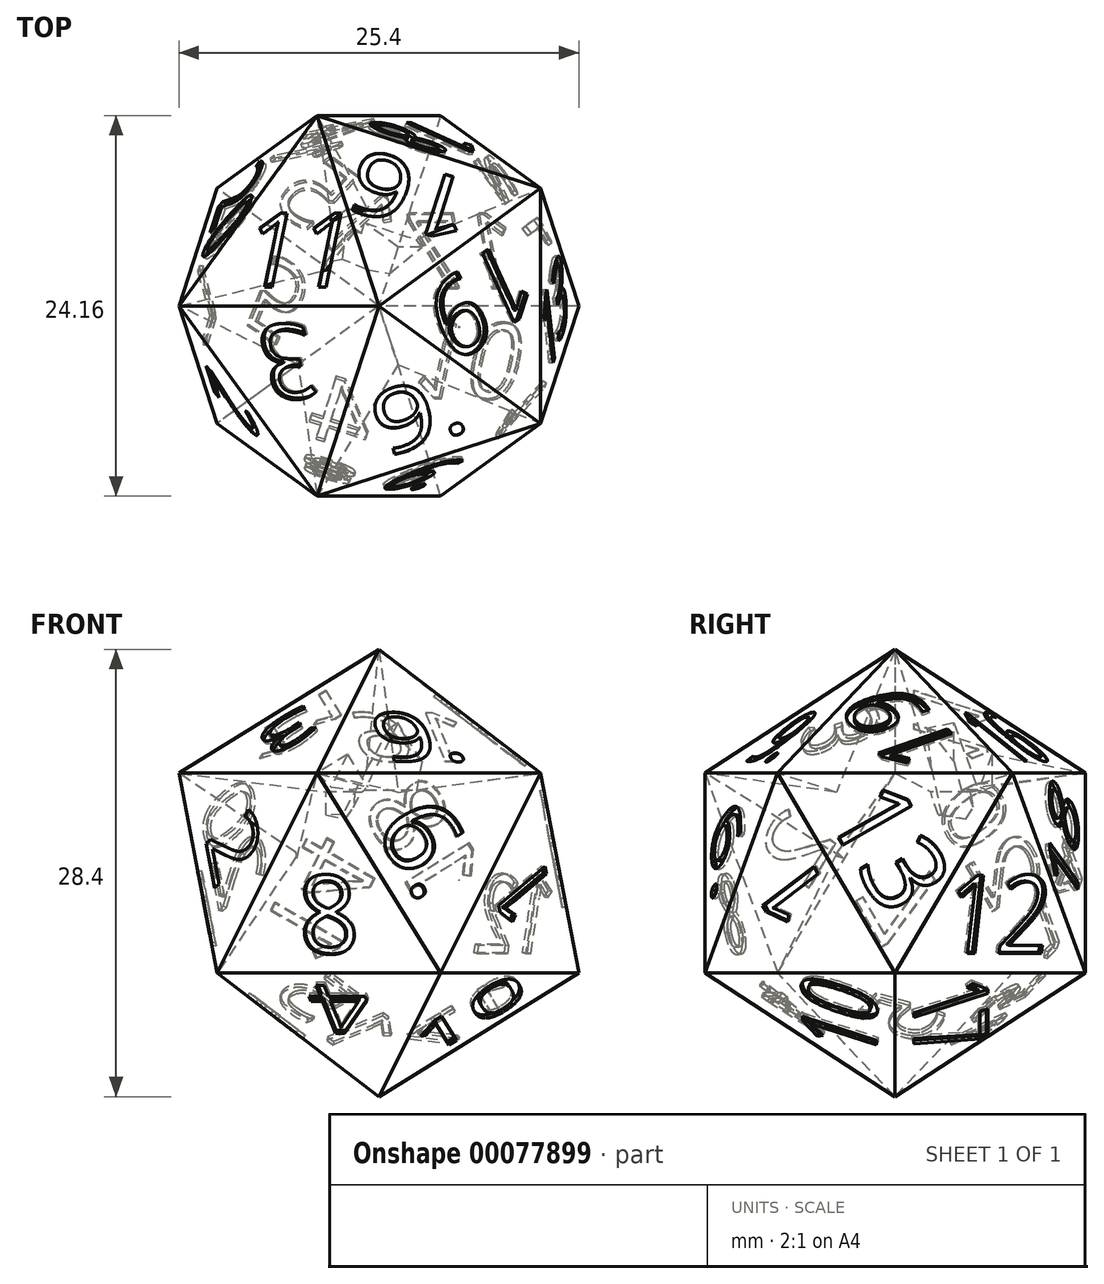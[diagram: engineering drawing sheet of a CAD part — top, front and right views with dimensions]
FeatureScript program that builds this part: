
annotation { "Feature Type Name" : "Feature", "Feature Type Description" : "" }
export const myFeature = defineFeature(function(context is Context, id is Id, definition is map)
    precondition{}
    {
        {
            var Q0;
            Q0=qCreatedBy(makeId("Top.planeOp"),FACE);
            var sketch = newSketch(context, id + "F0", { "sketchPlane" : qUnion([Q0])});
            skCircle(sketch, "E0.cCircle", {"center": v(0, 0) * mm, "radius": 12.7 * mm, "construction": true});
            skLineSegment(sketch, "E0.0", {"start": v(10.27, 7.46) * mm, "end": v(10.27, -7.46) * mm});
            skLineSegment(sketch, "E0.1", {"start": v(10.27, -7.46) * mm, "end": v(-3.92, -12.08) * mm});
            skLineSegment(sketch, "E0.2", {"start": v(-3.92, -12.08) * mm, "end": v(-12.7, 0) * mm});
            skLineSegment(sketch, "E0.3", {"start": v(-12.7, 0) * mm, "end": v(-3.92, 12.08) * mm});
            skLineSegment(sketch, "E0.4", {"start": v(-3.92, 12.08) * mm, "end": v(10.27, 7.46) * mm});
            skLineSegment(sketch, "E1", {"start": v(0, 0) * mm, "end": v(-3.92, -12.08) * mm, "construction": true});
            skSolve(sketch);
        }
        {
            var Q0;
            Q0=qCreatedBy(makeId("Right.planeOp"),FACE);
            var sketch = newSketch(context, id + "F1", { "sketchPlane" : qUnion([Q0])});
            skLineSegment(sketch, "E2", {"start": v(0, 0) * mm, "end": v(0, 7.85) * mm, "construction": true});
            skSolve(sketch);
        }
        {
            var Q0;
            Q0=sQuery(id+"F0.wireOp",VERTEX,"E0.1.start");
            var Q1;
            Q1=sQuery(id+"F0.wireOp",VERTEX,"E0.2.start");
            var Q2;
            Q2=sQuery(id+"F1.wireOp",VERTEX,"E2.end");
            cPlane(context, id + "F2", {"entities" : qUnion([Q0, Q1, Q2]), "cplaneType" : CPlaneType.THREE_POINT, "offset" : 152.4 * mm, "width" : 152.4 * mm, "height" : 152.4 * mm});
        }
        {
            var Q0;
            Q0=qCreatedBy(id+"F2.planeOp",FACE);
            var sketch = newSketch(context, id + "F3", { "sketchPlane" : qUnion([Q0])});
            skPoint(sketch, "E3.0", {"position": v(-5.19, -9.77) * mm});
            skPoint(sketch, "E4.0", {"position": v(9.27, -6.04) * mm});
            skPoint(sketch, "E5.0", {"position": v(-1.2, 4.61) * mm});
            skLineSegment(sketch, "E6", {"start": v(-5.19, -9.77) * mm, "end": v(-1.2, 4.61) * mm});
            skLineSegment(sketch, "E7", {"start": v(9.27, -6.04) * mm, "end": v(-1.2, 4.61) * mm});
            skLineSegment(sketch, "E8", {"start": v(9.27, -6.04) * mm, "end": v(-5.19, -9.77) * mm});
            skLineSegment(sketch, "E9", {"start": v(-3.19, -2.58) * mm, "end": v(9.27, -6.04) * mm, "construction": true});
            skSolve(sketch);
        }
        {
            var Q0;
            Q0=sQuery(id+"F3.wireOp",VERTEX,"E3.0");
            var Q1;
            Q1=sQuery(id+"F0.wireOp",VERTEX,"E0.2.end");
            var Q2;
            Q2=sQuery(id+"F1.wireOp",VERTEX,"E2.end");
            cPlane(context, id + "F4", {"entities" : qUnion([Q0, Q1, Q2]), "cplaneType" : CPlaneType.THREE_POINT, "offset" : 152.4 * mm, "width" : 152.4 * mm, "height" : 152.4 * mm});
        }
        {
            var Q0;
            Q0=qCreatedBy(id+"F4.planeOp",FACE);
            var sketch = newSketch(context, id + "F5", { "sketchPlane" : qUnion([Q0])});
            skPoint(sketch, "E10.0", {"position": v(-11.06, 0) * mm});
            skPoint(sketch, "E11.0", {"position": v(-0.99, -11.02) * mm});
            skPoint(sketch, "E12.0", {"position": v(3.52, 3.21) * mm});
            skLineSegment(sketch, "E13", {"start": v(-11.06, 0) * mm, "end": v(3.52, 3.21) * mm});
            skLineSegment(sketch, "E14", {"start": v(-0.99, -11.02) * mm, "end": v(-11.06, 0) * mm});
            skLineSegment(sketch, "E15", {"start": v(-0.99, -11.02) * mm, "end": v(3.52, 3.21) * mm});
            skLineSegment(sketch, "E16", {"start": v(-11.06, 0) * mm, "end": v(1.26, -3.9) * mm, "construction": true});
            skLineSegment(sketch, "E17", {"start": v(3.52, 3.21) * mm, "end": v(-6.03, -5.5) * mm, "construction": true});
            skSolve(sketch);
        }
        {
            var Q0;
            Q0=sQuery(id+"F5.wireOp",VERTEX,"E10.0");
            var Q1;
            Q1=sQuery(id+"F0.wireOp",VERTEX,"E0.3.end");
            var Q2;
            Q2=sQuery(id+"F3.wireOp",VERTEX,"E5.0");
            cPlane(context, id + "F6", {"entities" : qUnion([Q0, Q1, Q2]), "cplaneType" : CPlaneType.THREE_POINT, "offset" : 152.4 * mm, "width" : 152.4 * mm, "height" : 152.4 * mm});
        }
        {
            var Q0;
            Q0=qCreatedBy(id+"F6.planeOp",FACE);
            var sketch = newSketch(context, id + "F7", { "sketchPlane" : qUnion([Q0])});
            skPoint(sketch, "E18.0", {"position": v(-0.99, 11.02) * mm});
            skPoint(sketch, "E19.0", {"position": v(-11.06, 0) * mm});
            skPoint(sketch, "E20.0", {"position": v(3.52, -3.21) * mm});
            skLineSegment(sketch, "E21", {"start": v(-0.99, 11.02) * mm, "end": v(3.52, -3.21) * mm});
            skLineSegment(sketch, "E22", {"start": v(3.52, -3.21) * mm, "end": v(-11.06, 0) * mm});
            skLineSegment(sketch, "E23", {"start": v(-0.99, 11.02) * mm, "end": v(-11.06, 0) * mm});
            skLineSegment(sketch, "E24", {"start": v(-6.03, 5.5) * mm, "end": v(3.52, -3.21) * mm, "construction": true});
            skSolve(sketch);
        }
        {
            var Q0;
            Q0=sQuery(id+"F0.wireOp",VERTEX,"E0.4.end");
            var Q1;
            Q1=sQuery(id+"F3.wireOp",VERTEX,"E5.0");
            var Q2;
            Q2=sQuery(id+"F0.wireOp",VERTEX,"E0.3.end");
            cPlane(context, id + "F8", {"entities" : qUnion([Q0, Q1, Q2]), "cplaneType" : CPlaneType.THREE_POINT, "offset" : 152.4 * mm, "width" : 152.4 * mm, "height" : 152.4 * mm});
        }
        {
            var Q0;
            Q0=qCreatedBy(id+"F8.planeOp",FACE);
            var sketch = newSketch(context, id + "F9", { "sketchPlane" : qUnion([Q0])});
            skPoint(sketch, "E25.0", {"position": v(-5.19, 9.77) * mm});
            skPoint(sketch, "E26.0", {"position": v(9.27, 6.04) * mm});
            skPoint(sketch, "E27.0", {"position": v(-1.2, -4.61) * mm});
            skLineSegment(sketch, "E28", {"start": v(9.27, 6.04) * mm, "end": v(-1.2, -4.61) * mm});
            skLineSegment(sketch, "E29", {"start": v(-1.2, -4.61) * mm, "end": v(-5.19, 9.77) * mm});
            skLineSegment(sketch, "E30", {"start": v(-5.19, 9.77) * mm, "end": v(9.27, 6.04) * mm});
            skSolve(sketch);
        }
        {
            var Q0;
            Q0=sQuery(id+"F0.wireOp",VERTEX,"E0.4.end");
            var Q1;
            Q1=sQuery(id+"F3.wireOp",VERTEX,"E5.0");
            var Q2;
            Q2=sQuery(id+"F3.wireOp",VERTEX,"E4.0");
            cPlane(context, id + "F10", {"entities" : qUnion([Q0, Q1, Q2]), "cplaneType" : CPlaneType.THREE_POINT, "offset" : 152.4 * mm, "width" : 152.4 * mm, "height" : 152.4 * mm});
        }
        {
            var Q0;
            Q0=qCreatedBy(id+"F10.planeOp",FACE);
            var sketch = newSketch(context, id + "F11", { "sketchPlane" : qUnion([Q0])});
            skPoint(sketch, "E31.0", {"position": v(8.16, 7.46) * mm});
            skPoint(sketch, "E32.0", {"position": v(-4.76, 0) * mm});
            skPoint(sketch, "E33.0", {"position": v(8.16, -7.46) * mm});
            skLineSegment(sketch, "E34", {"start": v(8.16, 7.46) * mm, "end": v(8.16, -7.46) * mm});
            skLineSegment(sketch, "E35", {"start": v(8.16, -7.46) * mm, "end": v(-4.76, 0) * mm});
            skLineSegment(sketch, "E36", {"start": v(8.16, 7.46) * mm, "end": v(-4.76, 0) * mm});
            skSolve(sketch);
        }
        {
            var Q0;
            Q0=sQuery(id+"F5.wireOp",EDGE,"E14");
            cPlane(context, id + "F12", {"entities" : qUnion([Q0]), "cplaneType" : CPlaneType.LINE_ANGLE, "offset" : 152.4 * mm, "angle" : 100.81 * degree, "width" : 152.4 * mm, "height" : 152.4 * mm});
        }
        {
            var Q0;
            Q0=qCreatedBy(id+"F12.planeOp",FACE);
            var sketch = newSketch(context, id + "F13", { "sketchPlane" : qUnion([Q0])});
            skLineSegment(sketch, "E37", {"start": v(7.14, -2.92) * mm, "end": v(-7.66, -0.9) * mm});
            skPoint(sketch, "E38.orphan", {"position": v(-2, -14.73) * mm});
            skPoint(sketch, "E39.start.orphan", {"position": v(-0.26, -1.91) * mm});
            skPoint(sketch, "E40.start.orphan", {"position": v(2.56, -8.82) * mm});
            skLineSegment(sketch, "E41", {"start": v(7.14, -2.92) * mm, "end": v(-2, -14.72) * mm});
            skLineSegment(sketch, "E42", {"start": v(-7.66, -0.9) * mm, "end": v(-2, -14.72) * mm});
            skLineSegment(sketch, "E43", {"start": v(-0.26, -1.91) * mm, "end": v(-2, -14.72) * mm, "construction": true});
            skLineSegment(sketch, "E44", {"start": v(-4.83, -7.81) * mm, "end": v(7.14, -2.92) * mm, "construction": true});
            skSolve(sketch);
        }
        {
            var Q0;
            Q0=makeQuery(id+"F7.imprint","IMPRINT",FACE,{"disambiguationData":[TD([[makeQuery(id+"F7.imprint","IMPRINT",EDGE,{"derivedFrom":sQuery(id+"F7.wireOp",EDGE,"E21")}),-1.0]])]});
            extrude(context, id + "F14", {"entities" : qUnion([Q0]), "oppositeDirection" : true, "depth" : 2 / 76.2 * mm});
        }
        {
            var Q0;
            Q0=makeQuery(id+"F9.imprint","IMPRINT",FACE,{"disambiguationData":[TD([[makeQuery(id+"F9.imprint","IMPRINT",EDGE,{"derivedFrom":sQuery(id+"F9.wireOp",EDGE,"E28")}),-1.0]])]});
            extrude(context, id + "F15", {"entities" : qUnion([Q0]), "operationType" : NewBodyOperationType.ADD, "oppositeDirection" : true, "depth" : 2 / 76.2 * mm});
        }
        {
            var Q0;
            Q0=makeQuery(id+"F11.imprint","IMPRINT",FACE,{"disambiguationData":[TD([[makeQuery(id+"F11.imprint","IMPRINT",EDGE,{"derivedFrom":sQuery(id+"F11.wireOp",EDGE,"E34")}),-1.0]])]});
            extrude(context, id + "F16", {"entities" : qUnion([Q0]), "operationType" : NewBodyOperationType.ADD, "depth" : 16.93 * mm});
        }
        {
            var Q0;
            Q0=makeQuery(id+"F3.imprint","IMPRINT",FACE,{"disambiguationData":[TD([[makeQuery(id+"F3.imprint","IMPRINT",EDGE,{"derivedFrom":sQuery(id+"F3.wireOp",EDGE,"E6")}),-1.0]])]});
            extrude(context, id + "F17", {"entities" : qUnion([Q0]), "operationType" : NewBodyOperationType.ADD, "oppositeDirection" : true, "depth" : 2 / 76.2 * mm});
        }
        {
            var Q0;
            Q0=makeQuery(id+"F5.imprint","IMPRINT",FACE,{"disambiguationData":[TD([[makeQuery(id+"F5.imprint","IMPRINT",EDGE,{"derivedFrom":sQuery(id+"F5.wireOp",EDGE,"E13")}),-1.0]])]});
            extrude(context, id + "F18", {"entities" : qUnion([Q0]), "operationType" : NewBodyOperationType.ADD, "oppositeDirection" : true, "depth" : 18.55 * mm});
        }
        {
            var Q0;
            Q0=qSketchRegion(id+"F13",true);
            extrude(context, id + "F19", {"entities" : qUnion([Q0]), "operationType" : NewBodyOperationType.ADD, "depth" : 2 / 76.2 * mm});
        }
        {
            var Q0;
            Q0=makeQuery(id+"F19.opExtrude","CAP_EDGE",EDGE,{"disambiguationData":[OSD([sQuery(id+"F13.wireOp",EDGE,"E42")])],"isStart":true});
            cPlane(context, id + "F20", {"entities" : qUnion([Q0]), "cplaneType" : CPlaneType.LINE_ANGLE, "offset" : 152.4 * mm, "angle" : 100.81 * degree, "width" : 152.4 * mm, "height" : 152.4 * mm});
        }
        {
            var Q0;
            Q0=qCreatedBy(id+"F20.planeOp",FACE);
            var sketch = newSketch(context, id + "F21", { "sketchPlane" : qUnion([Q0])});
            skLineSegment(sketch, "E45.0", {"start": v(0.15, 2.38) * mm, "end": v(6.81, -10.98) * mm});
            skLineSegment(sketch, "E46", {"start": v(6.81, -10.98) * mm, "end": v(-8.1, -10.07) * mm});
            skLineSegment(sketch, "E47", {"start": v(-8.1, -10.07) * mm, "end": v(0.15, 2.38) * mm});
            skLineSegment(sketch, "E48", {"start": v(-8.1, -10.07) * mm, "end": v(3.48, -4.3) * mm, "construction": true});
            skSolve(sketch);
        }
        {
            var Q0;
            Q0=qSketchRegion(id+"F21",true);
            extrude(context, id + "F22", {"entities" : qUnion([Q0]), "operationType" : NewBodyOperationType.ADD, "depth" : 16.93 * mm});
        }
        {
            var Q0;
            Q0=sQuery(id+"F5.wireOp",VERTEX,"E11.0");
            var Q1;
            Q1=sQuery(id+"F3.wireOp",VERTEX,"E4.0");
            var Q2;
            Q2=makeQuery(id+"F22.opExtrude","CAP_VERTEX",VERTEX,{"disambiguationData":[OSD([sQuery(id+"F21.wireOp",EDGE,"E46"),sQuery(id+"F21.wireOp",EDGE,"E47")])],"isStart":true});
            cPlane(context, id + "F23", {"entities" : qUnion([Q0, Q1, Q2]), "cplaneType" : CPlaneType.THREE_POINT, "offset" : 152.4 * mm, "width" : 152.4 * mm, "height" : 152.4 * mm});
        }
        {
            var Q0;
            Q0=qCreatedBy(id+"F23.planeOp",FACE);
            var sketch = newSketch(context, id + "F24", { "sketchPlane" : qUnion([Q0])});
            skLineSegment(sketch, "E49.0", {"start": v(0.9, -14.83) * mm, "end": v(-7.33, -2.38) * mm});
            skLineSegment(sketch, "E50.0", {"start": v(7.57, -1.47) * mm, "end": v(-7.33, -2.38) * mm});
            skLineSegment(sketch, "E51", {"start": v(0.9, -14.83) * mm, "end": v(7.57, -1.47) * mm});
            skLineSegment(sketch, "E52", {"start": v(4.24, -8.15) * mm, "end": v(-7.33, -2.38) * mm, "construction": true});
            skSolve(sketch);
        }
        {
            var Q0;
            Q0=makeQuery(id+"F24.imprint","IMPRINT",FACE,{"disambiguationData":[TD([[makeQuery(id+"F24.imprint","IMPRINT",EDGE,{"derivedFrom":sQuery(id+"F24.wireOp",EDGE,"E49.0")}),-1.0]])]});
            extrude(context, id + "F25", {"entities" : qUnion([Q0]), "operationType" : NewBodyOperationType.ADD, "oppositeDirection" : true, "depth" : 16.93 * mm});
        }
        {
            var Q0;
            Q0=makeQuery(id+"F14.opExtrude","CAP_EDGE",EDGE,{"disambiguationData":[OSD([sQuery(id+"F7.wireOp",EDGE,"E23")])],"isStart":true});
            cPlane(context, id + "F26", {"entities" : qUnion([Q0]), "cplaneType" : CPlaneType.LINE_ANGLE, "offset" : 152.4 * mm, "angle" : 79.18 * degree, "width" : 152.4 * mm, "height" : 152.4 * mm});
        }
        {
            var Q0;
            Q0=qCreatedBy(id+"F26.planeOp",FACE);
            var sketch = newSketch(context, id + "F27", { "sketchPlane" : qUnion([Q0])});
            skLineSegment(sketch, "E53.0", {"start": v(7.66, -0.9) * mm, "end": v(-7.14, -2.92) * mm});
            skLineSegment(sketch, "E54", {"start": v(7.66, -0.9) * mm, "end": v(2, -14.72) * mm});
            skLineSegment(sketch, "E55", {"start": v(2, -14.72) * mm, "end": v(-7.14, -2.92) * mm});
            skLineSegment(sketch, "E56", {"start": v(2, -14.72) * mm, "end": v(0.26, -1.91) * mm, "construction": true});
            skLineSegment(sketch, "E57", {"start": v(4.83, -7.81) * mm, "end": v(-7.14, -2.92) * mm, "construction": true});
            skSolve(sketch);
        }
        {
            var Q0;
            Q0=qSketchRegion(id+"F27",true);
            extrude(context, id + "F28", {"entities" : qUnion([Q0]), "operationType" : NewBodyOperationType.ADD, "depth" : 6.35 * mm});
        }
        {
            var Q0;
            Q0=sQuery(id+"F7.wireOp",VERTEX,"E19.0");
            var Q1;
            Q1=makeQuery(id+"F22.boolean.opBoolean","MERGE",VERTEX,{"derivedFrom":[makeQuery(id+"F19.opExtrude","CAP_VERTEX",VERTEX,{"disambiguationData":[OSD([sQuery(id+"F13.wireOp",EDGE,"E41"),sQuery(id+"F13.wireOp",EDGE,"E42")])],"isStart":true}),makeQuery(id+"F22.opExtrude","CAP_VERTEX",VERTEX,{"disambiguationData":[OSD([sQuery(id+"F21.wireOp",EDGE,"E45.0"),sQuery(id+"F21.wireOp",EDGE,"E46")])],"isStart":true})]});
            var Q2;
            Q2=sQuery(id+"F27.wireOp",VERTEX,"E54.end");
            cPlane(context, id + "F29", {"entities" : qUnion([Q0, Q1, Q2]), "cplaneType" : CPlaneType.THREE_POINT, "offset" : 152.4 * mm, "width" : 152.4 * mm, "height" : 152.4 * mm});
        }
        {
            var Q0;
            Q0=qCreatedBy(id+"F29.planeOp",FACE);
            var sketch = newSketch(context, id + "F30", { "sketchPlane" : qUnion([Q0])});
            skLineSegment(sketch, "E58.0", {"start": v(0, 2.38) * mm, "end": v(7.46, -10.55) * mm});
            skLineSegment(sketch, "E59.0", {"start": v(-7.47, -10.55) * mm, "end": v(0, 2.38) * mm});
            skLineSegment(sketch, "E60", {"start": v(-7.47, -10.55) * mm, "end": v(7.46, -10.55) * mm});
            skSolve(sketch);
        }
        {
            var Q0;
            Q0=makeQuery(id+"F30.imprint","IMPRINT",FACE,{"disambiguationData":[TD([[makeQuery(id+"F30.imprint","IMPRINT",EDGE,{"derivedFrom":sQuery(id+"F30.wireOp",EDGE,"E58.0")}),-1.0]])]});
            extrude(context, id + "F31", {"entities" : qUnion([Q0]), "operationType" : NewBodyOperationType.ADD, "oppositeDirection" : true, "depth" : 6.35 * mm});
        }
        {
            var Q0;
            Q0=sQuery(id+"F27.wireOp",EDGE,"E54");
            cPlane(context, id + "F32", {"entities" : qUnion([Q0]), "cplaneType" : CPlaneType.LINE_ANGLE, "offset" : 152.4 * mm, "angle" : 79.19 * degree, "width" : 152.4 * mm, "height" : 152.4 * mm});
        }
        {
            var Q0;
            Q0=qCreatedBy(id+"F32.planeOp",FACE);
            var sketch = newSketch(context, id + "F33", { "sketchPlane" : qUnion([Q0])});
            skLineSegment(sketch, "E61.0", {"start": v(0.15, 2.38) * mm, "end": v(6.81, -10.98) * mm});
            skLineSegment(sketch, "E62", {"start": v(0.15, 2.38) * mm, "end": v(-8.1, -10.08) * mm});
            skLineSegment(sketch, "E63", {"start": v(-8.1, -10.08) * mm, "end": v(6.81, -10.98) * mm});
            skLineSegment(sketch, "E64", {"start": v(-8.1, -10.08) * mm, "end": v(3.48, -4.3) * mm, "construction": true});
            skLineSegment(sketch, "E65", {"start": v(0.15, 2.38) * mm, "end": v(-0.64, -10.53) * mm, "construction": true});
            skSolve(sketch);
        }
        {
            var Q0;
            Q0=qSketchRegion(id+"F33",true);
            extrude(context, id + "F34", {"entities" : qUnion([Q0]), "operationType" : NewBodyOperationType.ADD, "oppositeDirection" : true, "depth" : 6.35 * mm});
        }
        {
            var Q0;
            Q0=sQuery(id+"F33.wireOp",EDGE,"E63");
            cPlane(context, id + "F35", {"entities" : qUnion([Q0]), "cplaneType" : CPlaneType.LINE_ANGLE, "offset" : 152.4 * mm, "angle" : 52.62 * degree, "width" : 152.4 * mm, "height" : 152.4 * mm});
        }
        {
            var Q0;
            Q0=qCreatedBy(id+"F35.planeOp",FACE);
            var sketch = newSketch(context, id + "F36", { "sketchPlane" : qUnion([Q0])});
            skLineSegment(sketch, "E66.0", {"start": v(7.11, 2.3) * mm, "end": v(-7.34, -1.43) * mm});
            skLineSegment(sketch, "E67", {"start": v(7.11, 2.3) * mm, "end": v(3.12, -12.08) * mm});
            skLineSegment(sketch, "E68", {"start": v(3.12, -12.08) * mm, "end": v(-7.34, -1.43) * mm});
            skLineSegment(sketch, "E69", {"start": v(-0.11, 0.44) * mm, "end": v(3.12, -12.08) * mm, "construction": true});
            skLineSegment(sketch, "E70", {"start": v(-7.34, -1.43) * mm, "end": v(5.12, -4.89) * mm, "construction": true});
            skSolve(sketch);
        }
        {
            var Q0;
            Q0=qSketchRegion(id+"F36",true);
            extrude(context, id + "F37", {"entities" : qUnion([Q0]), "operationType" : NewBodyOperationType.ADD, "depth" : 6.35 * mm});
        }
        {
            var Q0;
            Q0=sQuery(id+"F36.wireOp",EDGE,"E67");
            cPlane(context, id + "F38", {"entities" : qUnion([Q0]), "cplaneType" : CPlaneType.LINE_ANGLE, "offset" : 152.4 * mm, "angle" : 30.6 * degree, "width" : 152.4 * mm, "height" : 152.4 * mm});
        }
        {
            var Q0;
            Q0=qCreatedBy(id+"F38.planeOp",FACE);
            var sketch = newSketch(context, id + "F39", { "sketchPlane" : qUnion([Q0])});
            skLineSegment(sketch, "E71.0", {"start": v(-4.7, -5.82) * mm, "end": v(-9.2, 8.42) * mm});
            skLineSegment(sketch, "E72", {"start": v(-4.7, -5.82) * mm, "end": v(5.37, 5.2) * mm});
            skLineSegment(sketch, "E73", {"start": v(5.37, 5.2) * mm, "end": v(-9.2, 8.42) * mm});
            skLineSegment(sketch, "E74", {"start": v(-6.96, 1.3) * mm, "end": v(5.37, 5.2) * mm, "construction": true});
            skSolve(sketch);
        }
        {
            var Q0;
            Q0=qSketchRegion(id+"F39",true);
            extrude(context, id + "F40", {"entities" : qUnion([Q0]), "operationType" : NewBodyOperationType.ADD, "oppositeDirection" : true, "depth" : 6.35 * mm});
        }
        {
            var Q0;
            Q0=sQuery(id+"F36.wireOp",VERTEX,"E66.0.start");
            var Q1;
            Q1=makeQuery(id+"F34.boolean.opBoolean","MERGE",VERTEX,{"derivedFrom":[makeQuery(id+"F28.boolean.opBoolean","MERGE",VERTEX,{"derivedFrom":[makeQuery(id+"F15.boolean.opBoolean","MERGE",VERTEX,{"derivedFrom":[makeQuery(id+"F14.opExtrude","CAP_VERTEX",VERTEX,{"disambiguationData":[OSD([sQuery(id+"F7.wireOp",EDGE,"E21"),sQuery(id+"F7.wireOp",EDGE,"E23")])],"isStart":true}),makeQuery(id+"F15.opExtrude","CAP_VERTEX",VERTEX,{"disambiguationData":[OSD([sQuery(id+"F9.wireOp",EDGE,"E29"),sQuery(id+"F9.wireOp",EDGE,"E30")])],"isStart":true})]}),makeQuery(id+"F28.opExtrude","CAP_VERTEX",VERTEX,{"disambiguationData":[OSD([sQuery(id+"F27.wireOp",EDGE,"E53.0"),sQuery(id+"F27.wireOp",EDGE,"E54")])],"isStart":true})]}),makeQuery(id+"F34.opExtrude","CAP_VERTEX",VERTEX,{"disambiguationData":[OSD([sQuery(id+"F33.wireOp",EDGE,"E61.0"),sQuery(id+"F33.wireOp",EDGE,"E62")])],"isStart":true})]});
            var Q2;
            Q2=makeQuery(id+"F16.boolean.opBoolean","MERGE",VERTEX,{"derivedFrom":[makeQuery(id+"F15.opExtrude","CAP_VERTEX",VERTEX,{"disambiguationData":[OSD([sQuery(id+"F9.wireOp",EDGE,"E28"),sQuery(id+"F9.wireOp",EDGE,"E30")])],"isStart":true}),makeQuery(id+"F16.opExtrude","CAP_VERTEX",VERTEX,{"disambiguationData":[OSD([sQuery(id+"F11.wireOp",EDGE,"E34"),sQuery(id+"F11.wireOp",EDGE,"E35")])],"isStart":true})]});
            cPlane(context, id + "F41", {"entities" : qUnion([Q0, Q1, Q2]), "cplaneType" : CPlaneType.THREE_POINT, "offset" : 152.4 * mm, "width" : 152.4 * mm, "height" : 152.4 * mm});
        }
        {
            var Q0;
            Q0=qCreatedBy(id+"F41.planeOp",FACE);
            var sketch = newSketch(context, id + "F42", { "sketchPlane" : qUnion([Q0])});
            skLineSegment(sketch, "E75.0", {"start": v(-7.33, -2.38) * mm, "end": v(7.57, -1.47) * mm});
            skLineSegment(sketch, "E76.0", {"start": v(-7.33, -2.38) * mm, "end": v(0.9, -14.83) * mm});
            skLineSegment(sketch, "E77", {"start": v(0.9, -14.83) * mm, "end": v(7.57, -1.47) * mm});
            skSolve(sketch);
        }
        {
            var Q0;
            Q0=qSketchRegion(id+"F42",true);
            extrude(context, id + "F43", {"entities" : qUnion([Q0]), "operationType" : NewBodyOperationType.ADD, "depth" : 6.35 * mm});
        }
        {
            var Q0;
            Q0=sQuery(id+"F36.wireOp",VERTEX,"E66.0.start");
            var Q1;
            Q1=makeQuery(id+"F40.opExtrude","CAP_VERTEX",VERTEX,{"disambiguationData":[OSD([sQuery(id+"F39.wireOp",EDGE,"E72"),sQuery(id+"F39.wireOp",EDGE,"E73")])],"isStart":true});
            var Q2;
            Q2=makeQuery(id+"F43.boolean.opBoolean","MERGE",VERTEX,{"derivedFrom":[makeQuery(id+"F16.boolean.opBoolean","MERGE",VERTEX,{"derivedFrom":[makeQuery(id+"F15.opExtrude","CAP_VERTEX",VERTEX,{"disambiguationData":[OSD([sQuery(id+"F9.wireOp",EDGE,"E28"),sQuery(id+"F9.wireOp",EDGE,"E30")])],"isStart":true}),makeQuery(id+"F16.opExtrude","CAP_VERTEX",VERTEX,{"disambiguationData":[OSD([sQuery(id+"F11.wireOp",EDGE,"E34"),sQuery(id+"F11.wireOp",EDGE,"E35")])],"isStart":true})]}),makeQuery(id+"F43.opExtrude","CAP_VERTEX",VERTEX,{"disambiguationData":[OSD([sQuery(id+"F42.wireOp",EDGE,"E75.0"),sQuery(id+"F42.wireOp",EDGE,"E77")])],"isStart":true})]});
            cPlane(context, id + "F44", {"entities" : qUnion([Q0, Q1, Q2]), "cplaneType" : CPlaneType.THREE_POINT, "offset" : 152.4 * mm, "width" : 152.4 * mm, "height" : 152.4 * mm});
        }
        {
            var Q0;
            Q0=qCreatedBy(id+"F44.planeOp",FACE);
            var sketch = newSketch(context, id + "F45", { "sketchPlane" : qUnion([Q0])});
            skLineSegment(sketch, "E78.0", {"start": v(5.97, -11.46) * mm, "end": v(0.32, 2.36) * mm});
            skLineSegment(sketch, "E79.0", {"start": v(5.97, -11.46) * mm, "end": v(-8.82, -9.44) * mm});
            skLineSegment(sketch, "E80", {"start": v(0.32, 2.36) * mm, "end": v(-8.82, -9.44) * mm});
            skSolve(sketch);
        }
        {
            var Q0;
            Q0=qSketchRegion(id+"F45",true);
            extrude(context, id + "F46", {"entities" : qUnion([Q0]), "operationType" : NewBodyOperationType.ADD, "oppositeDirection" : true, "depth" : 6.35 * mm});
        }
        {
            var Q0;
            Q0=makeQuery(id+"F46.boolean.opBoolean","MERGE",VERTEX,{"derivedFrom":[makeQuery(id+"F40.opExtrude","CAP_VERTEX",VERTEX,{"disambiguationData":[OSD([sQuery(id+"F39.wireOp",EDGE,"E72"),sQuery(id+"F39.wireOp",EDGE,"E73")])],"isStart":true}),makeQuery(id+"F46.opExtrude","CAP_VERTEX",VERTEX,{"disambiguationData":[OSD([sQuery(id+"F45.wireOp",EDGE,"E79.0"),sQuery(id+"F45.wireOp",EDGE,"E80")])],"isStart":true})]});
            var Q1;
            Q1=makeQuery(id+"F46.boolean.opBoolean","MERGE",VERTEX,{"derivedFrom":[makeQuery(id+"F43.boolean.opBoolean","MERGE",VERTEX,{"derivedFrom":[makeQuery(id+"F16.boolean.opBoolean","MERGE",VERTEX,{"derivedFrom":[makeQuery(id+"F15.opExtrude","CAP_VERTEX",VERTEX,{"disambiguationData":[OSD([sQuery(id+"F9.wireOp",EDGE,"E28"),sQuery(id+"F9.wireOp",EDGE,"E30")])],"isStart":true}),makeQuery(id+"F16.opExtrude","CAP_VERTEX",VERTEX,{"disambiguationData":[OSD([sQuery(id+"F11.wireOp",EDGE,"E34"),sQuery(id+"F11.wireOp",EDGE,"E35")])],"isStart":true})]}),makeQuery(id+"F43.opExtrude","CAP_VERTEX",VERTEX,{"disambiguationData":[OSD([sQuery(id+"F42.wireOp",EDGE,"E75.0"),sQuery(id+"F42.wireOp",EDGE,"E77")])],"isStart":true})]}),makeQuery(id+"F46.opExtrude","CAP_VERTEX",VERTEX,{"disambiguationData":[OSD([sQuery(id+"F45.wireOp",EDGE,"E78.0"),sQuery(id+"F45.wireOp",EDGE,"E80")])],"isStart":true})]});
            var Q2;
            Q2=makeQuery(id+"F25.boolean.opBoolean","MERGE",VERTEX,{"derivedFrom":[makeQuery(id+"F17.boolean.opBoolean","MERGE",VERTEX,{"derivedFrom":[makeQuery(id+"F16.opExtrude","CAP_VERTEX",VERTEX,{"disambiguationData":[OSD([sQuery(id+"F11.wireOp",EDGE,"E34"),sQuery(id+"F11.wireOp",EDGE,"E36")])],"isStart":true}),makeQuery(id+"F17.opExtrude","CAP_VERTEX",VERTEX,{"disambiguationData":[OSD([sQuery(id+"F3.wireOp",EDGE,"E7"),sQuery(id+"F3.wireOp",EDGE,"E8")])],"isStart":true})]}),makeQuery(id+"F25.opExtrude","CAP_VERTEX",VERTEX,{"disambiguationData":[OSD([sQuery(id+"F24.wireOp",EDGE,"E50.0"),sQuery(id+"F24.wireOp",EDGE,"E51")])],"isStart":true})]});
            cPlane(context, id + "F47", {"entities" : qUnion([Q0, Q1, Q2]), "cplaneType" : CPlaneType.THREE_POINT, "offset" : 152.4 * mm, "width" : 152.4 * mm, "height" : 152.4 * mm});
        }
        {
            var Q0;
            Q0=qCreatedBy(id+"F47.planeOp",FACE);
            var sketch = newSketch(context, id + "F48", { "sketchPlane" : qUnion([Q0])});
            skLineSegment(sketch, "E81.0", {"start": v(-7.46, -1.93) * mm, "end": v(0, -14.86) * mm});
            skLineSegment(sketch, "E82.0", {"start": v(7.46, -1.93) * mm, "end": v(-7.46, -1.93) * mm});
            skLineSegment(sketch, "E83", {"start": v(0, -14.86) * mm, "end": v(7.46, -1.93) * mm});
            skSolve(sketch);
        }
        {
            var Q0;
            Q0=qSketchRegion(id+"F48",true);
            extrude(context, id + "F49", {"entities" : qUnion([Q0]), "operationType" : NewBodyOperationType.ADD, "depth" : 6.35 * mm});
        }
        {
            var Q0;
            Q0=makeQuery(id+"F49.boolean.opBoolean","MERGE",VERTEX,{"derivedFrom":[makeQuery(id+"F46.boolean.opBoolean","MERGE",VERTEX,{"derivedFrom":[makeQuery(id+"F40.opExtrude","CAP_VERTEX",VERTEX,{"disambiguationData":[OSD([sQuery(id+"F39.wireOp",EDGE,"E72"),sQuery(id+"F39.wireOp",EDGE,"E73")])],"isStart":true}),makeQuery(id+"F46.opExtrude","CAP_VERTEX",VERTEX,{"disambiguationData":[OSD([sQuery(id+"F45.wireOp",EDGE,"E79.0"),sQuery(id+"F45.wireOp",EDGE,"E80")])],"isStart":true})]}),makeQuery(id+"F49.opExtrude","CAP_VERTEX",VERTEX,{"disambiguationData":[OSD([sQuery(id+"F48.wireOp",EDGE,"E81.0"),sQuery(id+"F48.wireOp",EDGE,"E83")])],"isStart":true})]});
            var Q1;
            Q1=makeQuery(id+"F49.boolean.opBoolean","MERGE",VERTEX,{"derivedFrom":[makeQuery(id+"F25.boolean.opBoolean","MERGE",VERTEX,{"derivedFrom":[makeQuery(id+"F17.boolean.opBoolean","MERGE",VERTEX,{"derivedFrom":[makeQuery(id+"F16.opExtrude","CAP_VERTEX",VERTEX,{"disambiguationData":[OSD([sQuery(id+"F11.wireOp",EDGE,"E34"),sQuery(id+"F11.wireOp",EDGE,"E36")])],"isStart":true}),makeQuery(id+"F17.opExtrude","CAP_VERTEX",VERTEX,{"disambiguationData":[OSD([sQuery(id+"F3.wireOp",EDGE,"E7"),sQuery(id+"F3.wireOp",EDGE,"E8")])],"isStart":true})]}),makeQuery(id+"F25.opExtrude","CAP_VERTEX",VERTEX,{"disambiguationData":[OSD([sQuery(id+"F24.wireOp",EDGE,"E50.0"),sQuery(id+"F24.wireOp",EDGE,"E51")])],"isStart":true})]}),makeQuery(id+"F49.opExtrude","CAP_VERTEX",VERTEX,{"disambiguationData":[OSD([sQuery(id+"F48.wireOp",EDGE,"E82.0"),sQuery(id+"F48.wireOp",EDGE,"E83")])],"isStart":true})]});
            var Q2;
            Q2=makeQuery(id+"F25.boolean.opBoolean","MERGE",VERTEX,{"derivedFrom":[makeQuery(id+"F22.opExtrude","CAP_VERTEX",VERTEX,{"disambiguationData":[OSD([sQuery(id+"F21.wireOp",EDGE,"E46"),sQuery(id+"F21.wireOp",EDGE,"E47")])],"isStart":true}),makeQuery(id+"F25.opExtrude","CAP_VERTEX",VERTEX,{"disambiguationData":[OSD([sQuery(id+"F24.wireOp",EDGE,"E49.0"),sQuery(id+"F24.wireOp",EDGE,"E51")])],"isStart":true})]});
            cPlane(context, id + "F50", {"entities" : qUnion([Q0, Q1, Q2]), "cplaneType" : CPlaneType.THREE_POINT, "offset" : 152.4 * mm, "width" : 152.4 * mm, "height" : 152.4 * mm});
        }
        {
            var Q0;
            Q0=qCreatedBy(id+"F50.planeOp",FACE);
            var sketch = newSketch(context, id + "F51", { "sketchPlane" : qUnion([Q0])});
            skLineSegment(sketch, "E84.0", {"start": v(-8.82, -9.44) * mm, "end": v(0.32, 2.36) * mm});
            skLineSegment(sketch, "E85.0", {"start": v(5.97, -11.46) * mm, "end": v(0.32, 2.36) * mm});
            skLineSegment(sketch, "E86", {"start": v(-8.82, -9.44) * mm, "end": v(5.97, -11.46) * mm});
            skSolve(sketch);
        }
        {
            var Q0;
            Q0=qSketchRegion(id+"F51",true);
            extrude(context, id + "F52", {"entities" : qUnion([Q0]), "operationType" : NewBodyOperationType.ADD, "depth" : 6.35 * mm});
        }
        {
            var Q0;
            Q0=makeQuery(id+"F52.boolean.opBoolean","MERGE",VERTEX,{"derivedFrom":[makeQuery(id+"F25.boolean.opBoolean","MERGE",VERTEX,{"derivedFrom":[makeQuery(id+"F22.opExtrude","CAP_VERTEX",VERTEX,{"disambiguationData":[OSD([sQuery(id+"F21.wireOp",EDGE,"E46"),sQuery(id+"F21.wireOp",EDGE,"E47")])],"isStart":true}),makeQuery(id+"F25.opExtrude","CAP_VERTEX",VERTEX,{"disambiguationData":[OSD([sQuery(id+"F24.wireOp",EDGE,"E49.0"),sQuery(id+"F24.wireOp",EDGE,"E51")])],"isStart":true})]}),makeQuery(id+"F52.opExtrude","CAP_VERTEX",VERTEX,{"disambiguationData":[OSD([sQuery(id+"F51.wireOp",EDGE,"E85.0"),sQuery(id+"F51.wireOp",EDGE,"E86")])],"isStart":true})]});
            var Q1;
            Q1=makeQuery(id+"F31.boolean.opBoolean","MERGE",VERTEX,{"derivedFrom":[makeQuery(id+"F22.boolean.opBoolean","MERGE",VERTEX,{"derivedFrom":[makeQuery(id+"F19.opExtrude","CAP_VERTEX",VERTEX,{"disambiguationData":[OSD([sQuery(id+"F13.wireOp",EDGE,"E41"),sQuery(id+"F13.wireOp",EDGE,"E42")])],"isStart":true}),makeQuery(id+"F22.opExtrude","CAP_VERTEX",VERTEX,{"disambiguationData":[OSD([sQuery(id+"F21.wireOp",EDGE,"E45.0"),sQuery(id+"F21.wireOp",EDGE,"E46")])],"isStart":true})]}),makeQuery(id+"F31.opExtrude","CAP_VERTEX",VERTEX,{"disambiguationData":[OSD([sQuery(id+"F30.wireOp",EDGE,"E58.0"),sQuery(id+"F30.wireOp",EDGE,"E60")])],"isStart":true})]});
            var Q2;
            Q2=sQuery(id+"F36.wireOp",VERTEX,"E69.end");
            cPlane(context, id + "F53", {"entities" : qUnion([Q0, Q1, Q2]), "cplaneType" : CPlaneType.THREE_POINT, "offset" : 152.4 * mm, "width" : 152.4 * mm, "height" : 152.4 * mm});
        }
        {
            var Q0;
            Q0=qCreatedBy(id+"F53.planeOp",FACE);
            var sketch = newSketch(context, id + "F54", { "sketchPlane" : qUnion([Q0])});
            skLineSegment(sketch, "E87.0", {"start": v(-7.34, 1.43) * mm, "end": v(7.11, -2.3) * mm});
            skLineSegment(sketch, "E88", {"start": v(7.11, -2.3) * mm, "end": v(3.12, 12.08) * mm});
            skLineSegment(sketch, "E89", {"start": v(3.12, 12.08) * mm, "end": v(-7.34, 1.43) * mm});
            skSolve(sketch);
        }
        {
            var Q0;
            Q0=qSketchRegion(id+"F54",true);
            extrude(context, id + "F55", {"entities" : qUnion([Q0]), "operationType" : NewBodyOperationType.ADD, "depth" : 6.35 * mm});
        }
        {
            var Q0;
            Q0=makeQuery(id+"F55.boolean.opBoolean","MERGE",VERTEX,{"derivedFrom":[makeQuery(id+"F52.boolean.opBoolean","MERGE",VERTEX,{"derivedFrom":[makeQuery(id+"F25.boolean.opBoolean","MERGE",VERTEX,{"derivedFrom":[makeQuery(id+"F22.opExtrude","CAP_VERTEX",VERTEX,{"disambiguationData":[OSD([sQuery(id+"F21.wireOp",EDGE,"E46"),sQuery(id+"F21.wireOp",EDGE,"E47")])],"isStart":true}),makeQuery(id+"F25.opExtrude","CAP_VERTEX",VERTEX,{"disambiguationData":[OSD([sQuery(id+"F24.wireOp",EDGE,"E49.0"),sQuery(id+"F24.wireOp",EDGE,"E51")])],"isStart":true})]}),makeQuery(id+"F52.opExtrude","CAP_VERTEX",VERTEX,{"disambiguationData":[OSD([sQuery(id+"F51.wireOp",EDGE,"E85.0"),sQuery(id+"F51.wireOp",EDGE,"E86")])],"isStart":true})]}),makeQuery(id+"F55.opExtrude","CAP_VERTEX",VERTEX,{"disambiguationData":[OSD([sQuery(id+"F54.wireOp",EDGE,"E87.0"),sQuery(id+"F54.wireOp",EDGE,"E88")])],"isStart":true})]});
            var Q1;
            Q1=makeQuery(id+"F52.boolean.opBoolean","MERGE",VERTEX,{"derivedFrom":[makeQuery(id+"F49.boolean.opBoolean","MERGE",VERTEX,{"derivedFrom":[makeQuery(id+"F46.boolean.opBoolean","MERGE",VERTEX,{"derivedFrom":[makeQuery(id+"F40.opExtrude","CAP_VERTEX",VERTEX,{"disambiguationData":[OSD([sQuery(id+"F39.wireOp",EDGE,"E72"),sQuery(id+"F39.wireOp",EDGE,"E73")])],"isStart":true}),makeQuery(id+"F46.opExtrude","CAP_VERTEX",VERTEX,{"disambiguationData":[OSD([sQuery(id+"F45.wireOp",EDGE,"E79.0"),sQuery(id+"F45.wireOp",EDGE,"E80")])],"isStart":true})]}),makeQuery(id+"F49.opExtrude","CAP_VERTEX",VERTEX,{"disambiguationData":[OSD([sQuery(id+"F48.wireOp",EDGE,"E81.0"),sQuery(id+"F48.wireOp",EDGE,"E83")])],"isStart":true})]}),makeQuery(id+"F52.opExtrude","CAP_VERTEX",VERTEX,{"disambiguationData":[OSD([sQuery(id+"F51.wireOp",EDGE,"E84.0"),sQuery(id+"F51.wireOp",EDGE,"E86")])],"isStart":true})]});
            var Q2;
            Q2=makeQuery(id+"F55.opExtrude","CAP_VERTEX",VERTEX,{"disambiguationData":[OSD([sQuery(id+"F54.wireOp",EDGE,"E88"),sQuery(id+"F54.wireOp",EDGE,"E89")])],"isStart":true});
            cPlane(context, id + "F56", {"entities" : qUnion([Q0, Q1, Q2]), "cplaneType" : CPlaneType.THREE_POINT, "offset" : 152.4 * mm, "width" : 152.4 * mm, "height" : 152.4 * mm});
        }
        {
            var Q0;
            Q0=qCreatedBy(id+"F56.planeOp",FACE);
            var sketch = newSketch(context, id + "F57", { "sketchPlane" : qUnion([Q0])});
            skLineSegment(sketch, "E90.0", {"start": v(-4.7, 5.82) * mm, "end": v(-9.2, -8.42) * mm});
            skPoint(sketch, "E91.0.end.orphan", {"position": v(-9.2, -8.42) * mm});
            skPoint(sketch, "E91.0.start.orphan", {"position": v(5.37, -5.2) * mm});
            skLineSegment(sketch, "E92", {"start": v(-4.7, 5.82) * mm, "end": v(5.37, -5.2) * mm});
            skLineSegment(sketch, "E93", {"start": v(5.37, -5.2) * mm, "end": v(-9.2, -8.42) * mm});
            skSolve(sketch);
        }
        {
            var Q0;
            Q0=qSketchRegion(id+"F57",true);
            extrude(context, id + "F58", {"entities" : qUnion([Q0]), "operationType" : NewBodyOperationType.ADD, "oppositeDirection" : true, "depth" : 6.35 * mm});
        }
        {
            var Q0;
            Q0=makeQuery(id+"F55.boolean.opBoolean","MERGE",VERTEX,{"derivedFrom":[makeQuery(id+"F31.boolean.opBoolean","MERGE",VERTEX,{"derivedFrom":[makeQuery(id+"F22.boolean.opBoolean","MERGE",VERTEX,{"derivedFrom":[makeQuery(id+"F19.opExtrude","CAP_VERTEX",VERTEX,{"disambiguationData":[OSD([sQuery(id+"F13.wireOp",EDGE,"E41"),sQuery(id+"F13.wireOp",EDGE,"E42")])],"isStart":true}),makeQuery(id+"F22.opExtrude","CAP_VERTEX",VERTEX,{"disambiguationData":[OSD([sQuery(id+"F21.wireOp",EDGE,"E45.0"),sQuery(id+"F21.wireOp",EDGE,"E46")])],"isStart":true})]}),makeQuery(id+"F31.opExtrude","CAP_VERTEX",VERTEX,{"disambiguationData":[OSD([sQuery(id+"F30.wireOp",EDGE,"E58.0"),sQuery(id+"F30.wireOp",EDGE,"E60")])],"isStart":true})]}),makeQuery(id+"F55.opExtrude","CAP_VERTEX",VERTEX,{"disambiguationData":[OSD([sQuery(id+"F54.wireOp",EDGE,"E87.0"),sQuery(id+"F54.wireOp",EDGE,"E89")])],"isStart":true})]});
            var Q1;
            Q1=sQuery(id+"F57.wireOp",VERTEX,"E91.0.end.orphan");
            var Q2;
            Q2=sQuery(id+"F36.wireOp",VERTEX,"E68.end");
            cPlane(context, id + "F59", {"entities" : qUnion([Q0, Q1, Q2]), "cplaneType" : CPlaneType.THREE_POINT, "offset" : 152.4 * mm, "width" : 152.4 * mm, "height" : 152.4 * mm});
        }
        {
            var Q0;
            Q0=qCreatedBy(id+"F59.planeOp",FACE);
            var sketch = newSketch(context, id + "F60", { "sketchPlane" : qUnion([Q0])});
            skLineSegment(sketch, "E94.0", {"start": v(12.48, 0) * mm, "end": v(-0.45, 7.46) * mm});
            skLineSegment(sketch, "E95", {"start": v(-0.45, 7.46) * mm, "end": v(-0.45, -7.47) * mm});
            skPoint(sketch, "E96.0.start.orphan", {"position": v(12.48, 0) * mm});
            skLineSegment(sketch, "E97", {"start": v(12.48, 0) * mm, "end": v(-0.45, -7.47) * mm});
            skSolve(sketch);
        }
        {
            var Q0;
            Q0=qSketchRegion(id+"F60",true);
            extrude(context, id + "F61", {"entities" : qUnion([Q0]), "operationType" : NewBodyOperationType.ADD, "oppositeDirection" : true, "depth" : 6.35 * mm});
        }
        {
            var Q0;
            Q0=makeQuery(id+"F28.opExtrude","CAP_FACE",FACE,{"disambiguationData":[OSD([sQuery(id+"F27.wireOp",EDGE,"E53.0"),sQuery(id+"F27.wireOp",EDGE,"E54"),sQuery(id+"F27.wireOp",EDGE,"E55")])],"isStart":true});
            var sketch = newSketch(context, id + "F62", { "sketchPlane" : qUnion([Q0])});
            skText(sketch, "E98", { "text": "20", "fontName": "OpenSans-Regular.ttf"});
            const initialGuessF62  = {"E98": [-0.0008, -0.0111, 0.61245, 0.79051, 0.00508]};
            skSetInitialGuess(sketch, initialGuessF62);
            skSolve(sketch);
        }
        {
            var Q0;
            Q0=makeQuery(id+"F14.opExtrude","CAP_FACE",FACE,{"disambiguationData":[OSD([sQuery(id+"F7.wireOp",EDGE,"E21"),sQuery(id+"F7.wireOp",EDGE,"E22"),sQuery(id+"F7.wireOp",EDGE,"E23")])],"isStart":true});
            var sketch = newSketch(context, id + "F63", { "sketchPlane" : qUnion([Q0])});
            skText(sketch, "E99", { "text": "11", "fontName": "OpenSans-Regular.ttf"});
            const initialGuessF63  = {"E99": [-0.00667, 0.00033, 0.97654, -0.21534, 0.00508]};
            skSetInitialGuess(sketch, initialGuessF63);
            skSolve(sketch);
        }
        {
            var Q0;
            Q0=makeQuery(id+"F15.opExtrude","CAP_FACE",FACE,{"disambiguationData":[OSD([sQuery(id+"F9.wireOp",EDGE,"E28"),sQuery(id+"F9.wireOp",EDGE,"E29"),sQuery(id+"F9.wireOp",EDGE,"E30")])],"isStart":true});
            var sketch = newSketch(context, id + "F64", { "sketchPlane" : qUnion([Q0])});
            skText(sketch, "E100", { "text": "16", "fontName": "OpenSans-Regular.ttf"});
            const initialGuessF64  = {"E100": [0.00546, 0.00571, -0.96824, 0.25, 0.00508]};
            skSetInitialGuess(sketch, initialGuessF64);
            skSolve(sketch);
        }
        {
            var Q0;
            Q0=makeQuery(id+"F43.opExtrude","CAP_FACE",FACE,{"disambiguationData":[OSD([sQuery(id+"F42.wireOp",EDGE,"E75.0"),sQuery(id+"F42.wireOp",EDGE,"E76.0"),sQuery(id+"F42.wireOp",EDGE,"E77")])],"isStart":true});
            var sketch = newSketch(context, id + "F65", { "sketchPlane" : qUnion([Q0])});
            skText(sketch, "E101", { "text": "18", "fontName": "OpenSans-Regular.ttf"});
            const initialGuessF65  = {"E101": [3e-05, -0.01112, 0.55168, 0.83405, 0.00508]};
            skSetInitialGuess(sketch, initialGuessF65);
            skSolve(sketch);
        }
        {
            var Q0;
            Q0=makeQuery(id+"F34.opExtrude","CAP_FACE",FACE,{"disambiguationData":[OSD([sQuery(id+"F33.wireOp",EDGE,"E61.0"),sQuery(id+"F33.wireOp",EDGE,"E62"),sQuery(id+"F33.wireOp",EDGE,"E63")])],"isStart":true});
            var sketch = newSketch(context, id + "F66", { "sketchPlane" : qUnion([Q0])});
            skText(sketch, "E102", { "text": "14\n", "fontName": "OpenSans-Regular.ttf"});
            const initialGuessF66  = {"E102": [0.00411, -0.00842, -0.44648, 0.8948, 0.00508]};
            skSetInitialGuess(sketch, initialGuessF66);
            skSolve(sketch);
        }
        {
            var Q0;
            Q0=makeQuery(id+"F18.opExtrude","CAP_FACE",FACE,{"disambiguationData":[OSD([sQuery(id+"F5.wireOp",EDGE,"E13"),sQuery(id+"F5.wireOp",EDGE,"E14"),sQuery(id+"F5.wireOp",EDGE,"E15")])],"isStart":true});
            var sketch = newSketch(context, id + "F67", { "sketchPlane" : qUnion([Q0])});
            skText(sketch, "E103", { "text": "3\n", "fontName": "OpenSans-Regular.ttf"});
            const initialGuessF67  = {"E103": [-0.00173, 0.00076, -0.97654, -0.21534, 0.00508]};
            skSetInitialGuess(sketch, initialGuessF67);
            skSolve(sketch);
        }
        {
            var Q0;
            Q0=makeQuery(id+"F16.opExtrude","CAP_FACE",FACE,{"disambiguationData":[OSD([sQuery(id+"F11.wireOp",EDGE,"E34"),sQuery(id+"F11.wireOp",EDGE,"E35"),sQuery(id+"F11.wireOp",EDGE,"E36")])],"isStart":true});
            var sketch = newSketch(context, id + "F68", { "sketchPlane" : qUnion([Q0])});
            skText(sketch, "E104", { "text": "19", "fontName": "OpenSans-Regular.ttf"});
            const initialGuessF68  = {"E104": [0.00566, 0.00455, -0.86602, -0.5, 0.00508]};
            skSetInitialGuess(sketch, initialGuessF68);
            skSolve(sketch);
        }
        {
            var Q0;
            Q0=makeQuery(id+"F46.opExtrude","CAP_FACE",FACE,{"disambiguationData":[OSD([sQuery(id+"F45.wireOp",EDGE,"E78.0"),sQuery(id+"F45.wireOp",EDGE,"E79.0"),sQuery(id+"F45.wireOp",EDGE,"E80")])],"isStart":true});
            var sketch = newSketch(context, id + "F69", { "sketchPlane" : qUnion([Q0])});
            skText(sketch, "E105", { "text": "12", "fontName": "OpenSans-Regular.ttf"});
            const initialGuessF69  = {"E105": [-0.00506, -0.00867, 0.99084, -0.13504, 0.00508]};
            skSetInitialGuess(sketch, initialGuessF69);
            skSolve(sketch);
        }
        {
            var Q0;
            Q0=makeQuery(id+"F37.opExtrude","CAP_FACE",FACE,{"disambiguationData":[OSD([sQuery(id+"F36.wireOp",EDGE,"E66.0"),sQuery(id+"F36.wireOp",EDGE,"E67"),sQuery(id+"F36.wireOp",EDGE,"E68")])],"isStart":true});
            var sketch = newSketch(context, id + "F70", { "sketchPlane" : qUnion([Q0])});
            skSolve(sketch);
        }
        {
            var Q0;
            Q0=makeQuery(id+"F70.imprint","IMPRINT",FACE,{"disambiguationData":[TD([[makeQuery(id+"F70.imprint","IMPRINT",EDGE,{"derivedFrom":makeQuery(id+"F37.opExtrude","CAP_EDGE",EDGE,{"disambiguationData":[OSD([sQuery(id+"F36.wireOp",EDGE,"E68")])],"isStart":true})}),1.0]])]});
            var sketch = newSketch(context, id + "F71", { "sketchPlane" : qUnion([Q0])});
            skText(sketch, "E106", { "text": "15", "fontName": "OpenSans-Regular.ttf"});
            const initialGuessF71  = {"E106": [0.00148, 0.0086, -0.70055, -0.7136, 0.00508]};
            skSetInitialGuess(sketch, initialGuessF71);
            skSolve(sketch);
        }
        {
            var Q0;
            Q0=makeQuery(id+"F31.opExtrude","CAP_FACE",FACE,{"disambiguationData":[OSD([sQuery(id+"F30.wireOp",EDGE,"E58.0"),sQuery(id+"F30.wireOp",EDGE,"E59.0"),sQuery(id+"F30.wireOp",EDGE,"E60")])],"isStart":true});
            var sketch = newSketch(context, id + "F72", { "sketchPlane" : qUnion([Q0])});
            skText(sketch, "E107", { "text": "7", "fontName": "OpenSans-Regular.ttf"});
            const initialGuessF72  = {"E107": [-0.00171, -0.00313, -0.50007, -0.86599, 0.00508]};
            skSetInitialGuess(sketch, initialGuessF72);
            skSolve(sketch);
        }
        {
            var Q0;
            Q0=makeQuery(id+"F61.opExtrude","CAP_FACE",FACE,{"disambiguationData":[OSD([sQuery(id+"F60.wireOp",EDGE,"E94.0"),sQuery(id+"F60.wireOp",EDGE,"E95"),sQuery(id+"F60.wireOp",EDGE,"E97")])],"isStart":true});
            var sketch = newSketch(context, id + "F73", { "sketchPlane" : qUnion([Q0])});
            skText(sketch, "E108", { "text": "5", "fontName": "OpenSans-Regular.ttf"});
            const initialGuessF73  = {"E108": [0.0038, -0.00354, 0.86603, 0.5, 0.00508]};
            skSetInitialGuess(sketch, initialGuessF73);
            skSolve(sketch);
        }
        {
            var Q0;
            Q0=makeQuery(id+"F55.opExtrude","CAP_FACE",FACE,{"disambiguationData":[OSD([sQuery(id+"F54.wireOp",EDGE,"E87.0"),sQuery(id+"F54.wireOp",EDGE,"E88"),sQuery(id+"F54.wireOp",EDGE,"E89")])],"isStart":true});
            var sketch = newSketch(context, id + "F74", { "sketchPlane" : qUnion([Q0])});
            skText(sketch, "E109", { "text": "4", "fontName": "OpenSans-Regular.ttf"});
            const initialGuessF74  = {"E109": [0.00209, -0.0003, -0.96826, -0.24996, 0.00508]};
            skSetInitialGuess(sketch, initialGuessF74);
            skSolve(sketch);
        }
        {
            var Q0;
            Q0=makeQuery(id+"F22.opExtrude","CAP_FACE",FACE,{"disambiguationData":[OSD([sQuery(id+"F21.wireOp",EDGE,"E45.0"),sQuery(id+"F21.wireOp",EDGE,"E46"),sQuery(id+"F21.wireOp",EDGE,"E47")])],"isStart":true});
            var sketch = newSketch(context, id + "F75", { "sketchPlane" : qUnion([Q0])});
            skText(sketch, "E110", { "text": "8", "fontName": "OpenSans-Regular.ttf"});
            const initialGuessF75  = {"E110": [-0.00127, -0.00937, 0.99815, 0.0608, 0.00508]};
            skSetInitialGuess(sketch, initialGuessF75);
            skSolve(sketch);
        }
        {
            var Q0;
            Q0=makeQuery(id+"F19.opExtrude","CAP_FACE",FACE,{"disambiguationData":[OSD([sQuery(id+"F13.wireOp",EDGE,"E37"),sQuery(id+"F13.wireOp",EDGE,"E41"),sQuery(id+"F13.wireOp",EDGE,"E42")])],"isStart":true});
            var sketch = newSketch(context, id + "F76", { "sketchPlane" : qUnion([Q0])});
            skText(sketch, "E111", { "text": "2", "fontName": "OpenSans-Regular.ttf"});
            const initialGuessF76  = {"E111": [-0.00268, -0.0066, 0.6124, -0.79055, 0.00508]};
            skSetInitialGuess(sketch, initialGuessF76);
            skSolve(sketch);
        }
        {
            var Q0;
            Q0=makeQuery(id+"F25.opExtrude","CAP_FACE",FACE,{"disambiguationData":[OSD([sQuery(id+"F24.wireOp",EDGE,"E49.0"),sQuery(id+"F24.wireOp",EDGE,"E50.0"),sQuery(id+"F24.wireOp",EDGE,"E51")])],"isStart":true});
            var sketch = newSketch(context, id + "F77", { "sketchPlane" : qUnion([Q0])});
            skText(sketch, "E112", { "text": "6.", "fontName": "OpenSans-Regular.ttf"});
            const initialGuessF77  = {"E112": [-0.00364, -0.00566, 0.55174, -0.83402, 0.00508]};
            skSetInitialGuess(sketch, initialGuessF77);
            skSolve(sketch);
        }
        {
            var Q0;
            Q0=makeQuery(id+"F17.opExtrude","CAP_FACE",FACE,{"disambiguationData":[OSD([sQuery(id+"F3.wireOp",EDGE,"E6"),sQuery(id+"F3.wireOp",EDGE,"E7"),sQuery(id+"F3.wireOp",EDGE,"E8")])],"isStart":true});
            var sketch = newSketch(context, id + "F78", { "sketchPlane" : qUnion([Q0])});
            skText(sketch, "E113", { "text": "9.", "fontName": "OpenSans-Regular.ttf"});
            const initialGuessF78  = {"E113": [-0.00088, -0.00735, 0.96824, 0.25, 0.00508]};
            skSetInitialGuess(sketch, initialGuessF78);
            skSolve(sketch);
        }
        {
            var Q0;
            Q0=makeQuery(id+"F52.opExtrude","CAP_FACE",FACE,{"disambiguationData":[OSD([sQuery(id+"F51.wireOp",EDGE,"E84.0"),sQuery(id+"F51.wireOp",EDGE,"E85.0"),sQuery(id+"F51.wireOp",EDGE,"E86")])],"isStart":true});
            var sketch = newSketch(context, id + "F79", { "sketchPlane" : qUnion([Q0])});
            skText(sketch, "E114", { "text": "1", "fontName": "OpenSans-Regular.ttf"});
            const initialGuessF79  = {"E114": [0.004, -0.0053, -0.61228, 0.79064, 0.00508]};
            skSetInitialGuess(sketch, initialGuessF79);
            skSolve(sketch);
        }
        {
            var Q0;
            Q0=makeQuery(id+"F49.opExtrude","CAP_FACE",FACE,{"disambiguationData":[OSD([sQuery(id+"F48.wireOp",EDGE,"E81.0"),sQuery(id+"F48.wireOp",EDGE,"E82.0"),sQuery(id+"F48.wireOp",EDGE,"E83")])],"isStart":true});
            var sketch = newSketch(context, id + "F80", { "sketchPlane" : qUnion([Q0])});
            skText(sketch, "E115", { "text": "13", "fontName": "OpenSans-Regular.ttf"});
            const initialGuessF80  = {"E115": [-0.00455, -0.00444, 0.49995, -0.86605, 0.00508]};
            skSetInitialGuess(sketch, initialGuessF80);
            skSolve(sketch);
        }
        {
            var Q0;
            Q0=makeQuery(id+"F58.opExtrude","CAP_FACE",FACE,{"disambiguationData":[OSD([sQuery(id+"F57.wireOp",EDGE,"E90.0"),sQuery(id+"F57.wireOp",EDGE,"E92"),sQuery(id+"F57.wireOp",EDGE,"E93")])],"isStart":true});
            var sketch = newSketch(context, id + "F81", { "sketchPlane" : qUnion([Q0])});
            skText(sketch, "E116", { "text": "10", "fontName": "OpenSans-Regular.ttf"});
            const initialGuessF81  = {"E116": [-0.00596, -0.0064, 0.97653, 0.21539, 0.00508]};
            skSetInitialGuess(sketch, initialGuessF81);
            skSolve(sketch);
        }
        {
            var Q0;
            Q0=makeQuery(id+"F40.opExtrude","CAP_FACE",FACE,{"disambiguationData":[OSD([sQuery(id+"F39.wireOp",EDGE,"E71.0"),sQuery(id+"F39.wireOp",EDGE,"E72"),sQuery(id+"F39.wireOp",EDGE,"E73")])],"isStart":true});
            var sketch = newSketch(context, id + "F82", { "sketchPlane" : qUnion([Q0])});
            skText(sketch, "E117", { "text": "17", "fontName": "OpenSans-Regular.ttf"});
            const initialGuessF82  = {"E117": [0.00157, 0.00474, -0.97654, 0.21531, 0.00508]};
            skSetInitialGuess(sketch, initialGuessF82);
            skSolve(sketch);
        }
        {
            var Q0;
            Q0=makeQuery(id+"F81.imprint","IMPRINT",FACE,{"disambiguationData":[TD([[makeQuery(id+"F81.imprint","IMPRINT",EDGE,{"derivedFrom":sQuery(id+"F81.wireOp",EDGE,"E116.sketch_text.stroke-9")}),-1.0]])]});
            var Q1;
            Q1=makeQuery(id+"F81.imprint","IMPRINT",FACE,{"disambiguationData":[TD([[makeQuery(id+"F81.imprint","IMPRINT",EDGE,{"derivedFrom":sQuery(id+"F81.wireOp",EDGE,"E116.sketch_text.stroke-0")}),-1.0]])]});
            extrude(context, id + "F83", {"entities" : qUnion([Q0, Q1]), "operationType" : NewBodyOperationType.REMOVE, "oppositeDirection" : true, "depth" : 0.25 * mm});
        }
        {
            var Q0;
            Q0=makeQuery(id+"F82.imprint","IMPRINT",FACE,{"disambiguationData":[TD([[makeQuery(id+"F82.imprint","IMPRINT",EDGE,{"derivedFrom":sQuery(id+"F82.wireOp",EDGE,"E117.sketch_text.stroke-0")}),-1.0]])]});
            var Q1;
            Q1=makeQuery(id+"F82.imprint","IMPRINT",FACE,{"disambiguationData":[TD([[makeQuery(id+"F82.imprint","IMPRINT",EDGE,{"derivedFrom":sQuery(id+"F82.wireOp",EDGE,"E117.sketch_text.stroke-9")}),-1.0]])]});
            extrude(context, id + "F84", {"entities" : qUnion([Q0, Q1]), "operationType" : NewBodyOperationType.REMOVE, "oppositeDirection" : true, "depth" : 0.25 * mm});
        }
        {
            var Q0;
            Q0=makeQuery(id+"F71.imprint","IMPRINT",FACE,{"disambiguationData":[TD([[makeQuery(id+"F71.imprint","IMPRINT",EDGE,{"derivedFrom":sQuery(id+"F71.wireOp",EDGE,"E106.sketch_text.stroke-0")}),-1.0]])]});
            var Q1;
            Q1=makeQuery(id+"F71.imprint","IMPRINT",FACE,{"disambiguationData":[TD([[makeQuery(id+"F71.imprint","IMPRINT",EDGE,{"derivedFrom":sQuery(id+"F71.wireOp",EDGE,"E106.sketch_text.stroke-9")}),-1.0]])]});
            extrude(context, id + "F85", {"entities" : qUnion([Q0, Q1]), "operationType" : NewBodyOperationType.REMOVE, "oppositeDirection" : true, "depth" : 0.25 * mm});
        }
        {
            var Q0;
            Q0=makeQuery(id+"F73.imprint","IMPRINT",FACE,{"disambiguationData":[TD([[makeQuery(id+"F73.imprint","IMPRINT",EDGE,{"derivedFrom":sQuery(id+"F73.wireOp",EDGE,"E108.sketch_text.stroke-0")}),-1.0]])]});
            extrude(context, id + "F86", {"entities" : qUnion([Q0]), "operationType" : NewBodyOperationType.REMOVE, "oppositeDirection" : true, "depth" : 0.25 * mm});
        }
        {
            var Q0;
            Q0=makeQuery(id+"F74.imprint","IMPRINT",FACE,{"disambiguationData":[TD([[makeQuery(id+"F74.imprint","IMPRINT",EDGE,{"derivedFrom":sQuery(id+"F74.wireOp",EDGE,"E109.sketch_text.stroke-0")}),-1.0]])]});
            extrude(context, id + "F87", {"entities" : qUnion([Q0]), "operationType" : NewBodyOperationType.REMOVE, "oppositeDirection" : true, "depth" : 0.25 * mm});
        }
        {
            var Q0;
            Q0=makeQuery(id+"F75.imprint","IMPRINT",FACE,{"disambiguationData":[TD([[makeQuery(id+"F75.imprint","IMPRINT",EDGE,{"derivedFrom":sQuery(id+"F75.wireOp",EDGE,"E110.sketch_text.stroke-0")}),-1.0]])]});
            extrude(context, id + "F88", {"entities" : qUnion([Q0]), "operationType" : NewBodyOperationType.REMOVE, "oppositeDirection" : true, "depth" : 0.25 * mm});
        }
        {
            var Q0;
            Q0=makeQuery(id+"F77.imprint","IMPRINT",FACE,{"disambiguationData":[TD([[makeQuery(id+"F77.imprint","IMPRINT",EDGE,{"derivedFrom":sQuery(id+"F77.wireOp",EDGE,"E112.sketch_text.stroke-0")}),-1.0]])]});
            var Q1;
            Q1=makeQuery(id+"F77.imprint","IMPRINT",FACE,{"disambiguationData":[TD([[makeQuery(id+"F77.imprint","IMPRINT",EDGE,{"derivedFrom":sQuery(id+"F77.wireOp",EDGE,"E112.sketch_text.stroke-25")}),-1.0]])]});
            extrude(context, id + "F89", {"entities" : qUnion([Q0, Q1]), "operationType" : NewBodyOperationType.REMOVE, "oppositeDirection" : true, "depth" : 0.25 * mm});
        }
        {
            var Q0;
            Q0=makeQuery(id+"F79.imprint","IMPRINT",FACE,{"disambiguationData":[TD([[makeQuery(id+"F79.imprint","IMPRINT",EDGE,{"derivedFrom":sQuery(id+"F79.wireOp",EDGE,"E114.sketch_text.stroke-0")}),-1.0]])]});
            extrude(context, id + "F90", {"entities" : qUnion([Q0]), "operationType" : NewBodyOperationType.REMOVE, "oppositeDirection" : true, "depth" : 0.25 * mm});
        }
        {
            var Q0;
            Q0=makeQuery(id+"F69.imprint","IMPRINT",FACE,{"disambiguationData":[TD([[makeQuery(id+"F69.imprint","IMPRINT",EDGE,{"derivedFrom":sQuery(id+"F69.wireOp",EDGE,"E105.sketch_text.stroke-0")}),-1.0]])]});
            var Q1;
            Q1=makeQuery(id+"F69.imprint","IMPRINT",FACE,{"disambiguationData":[TD([[makeQuery(id+"F69.imprint","IMPRINT",EDGE,{"derivedFrom":sQuery(id+"F69.wireOp",EDGE,"E105.sketch_text.stroke-9")}),-1.0]])]});
            extrude(context, id + "F91", {"entities" : qUnion([Q0, Q1]), "operationType" : NewBodyOperationType.REMOVE, "oppositeDirection" : true, "depth" : 0.28 * mm});
        }
        {
            var Q0;
            Q0=makeQuery(id+"F80.imprint","IMPRINT",FACE,{"disambiguationData":[TD([[makeQuery(id+"F80.imprint","IMPRINT",EDGE,{"derivedFrom":sQuery(id+"F80.wireOp",EDGE,"E115.sketch_text.stroke-9")}),-1.0]])]});
            var Q1;
            Q1=makeQuery(id+"F80.imprint","IMPRINT",FACE,{"disambiguationData":[TD([[makeQuery(id+"F80.imprint","IMPRINT",EDGE,{"derivedFrom":sQuery(id+"F80.wireOp",EDGE,"E115.sketch_text.stroke-0")}),-1.0]])]});
            extrude(context, id + "F92", {"entities" : qUnion([Q0, Q1]), "operationType" : NewBodyOperationType.REMOVE, "oppositeDirection" : true, "depth" : 0.25 * mm});
        }
        {
            var Q0;
            Q0=makeQuery(id+"F65.imprint","IMPRINT",FACE,{"disambiguationData":[TD([[makeQuery(id+"F65.imprint","IMPRINT",EDGE,{"derivedFrom":sQuery(id+"F65.wireOp",EDGE,"E101.sketch_text.stroke-9")}),-1.0]])]});
            var Q1;
            Q1=makeQuery(id+"F65.imprint","IMPRINT",FACE,{"disambiguationData":[TD([[makeQuery(id+"F65.imprint","IMPRINT",EDGE,{"derivedFrom":sQuery(id+"F65.wireOp",EDGE,"E101.sketch_text.stroke-0")}),-1.0]])]});
            extrude(context, id + "F93", {"entities" : qUnion([Q0, Q1]), "operationType" : NewBodyOperationType.REMOVE, "oppositeDirection" : true, "depth" : 0.25 * mm});
        }
        {
            var Q0;
            Q0=makeQuery(id+"F66.imprint","IMPRINT",FACE,{"disambiguationData":[TD([[makeQuery(id+"F66.imprint","IMPRINT",EDGE,{"derivedFrom":sQuery(id+"F66.wireOp",EDGE,"E102.sketch_text.stroke-0")}),-1.0]])]});
            var Q1;
            Q1=makeQuery(id+"F66.imprint","IMPRINT",FACE,{"disambiguationData":[TD([[makeQuery(id+"F66.imprint","IMPRINT",EDGE,{"derivedFrom":sQuery(id+"F66.wireOp",EDGE,"E102.sketch_text.stroke-9")}),-1.0]])]});
            extrude(context, id + "F94", {"entities" : qUnion([Q0, Q1]), "operationType" : NewBodyOperationType.REMOVE, "oppositeDirection" : true, "depth" : 0.25 * mm});
        }
        {
            var Q0;
            Q0=makeQuery(id+"F62.imprint","IMPRINT",FACE,{"disambiguationData":[TD([[makeQuery(id+"F62.imprint","IMPRINT",EDGE,{"derivedFrom":sQuery(id+"F62.wireOp",EDGE,"E98.sketch_text.stroke-0")}),-1.0]])]});
            var Q1;
            Q1=makeQuery(id+"F62.imprint","IMPRINT",FACE,{"disambiguationData":[TD([[makeQuery(id+"F62.imprint","IMPRINT",EDGE,{"derivedFrom":sQuery(id+"F62.wireOp",EDGE,"E98.sketch_text.stroke-20")}),-1.0]])]});
            extrude(context, id + "F95", {"entities" : qUnion([Q0, Q1]), "operationType" : NewBodyOperationType.REMOVE, "oppositeDirection" : true, "depth" : 0.25 * mm});
        }
        {
            var Q0;
            Q0=makeQuery(id+"F64.imprint","IMPRINT",FACE,{"disambiguationData":[TD([[makeQuery(id+"F64.imprint","IMPRINT",EDGE,{"derivedFrom":sQuery(id+"F64.wireOp",EDGE,"E100.sketch_text.stroke-9")}),-1.0]])]});
            var Q1;
            Q1=makeQuery(id+"F64.imprint","IMPRINT",FACE,{"disambiguationData":[TD([[makeQuery(id+"F64.imprint","IMPRINT",EDGE,{"derivedFrom":sQuery(id+"F64.wireOp",EDGE,"E100.sketch_text.stroke-0")}),-1.0]])]});
            extrude(context, id + "F96", {"entities" : qUnion([Q0, Q1]), "operationType" : NewBodyOperationType.REMOVE, "oppositeDirection" : true, "depth" : 0.25 * mm});
        }
        {
            var Q0;
            Q0=makeQuery(id+"F63.imprint","IMPRINT",FACE,{"disambiguationData":[TD([[makeQuery(id+"F63.imprint","IMPRINT",EDGE,{"derivedFrom":sQuery(id+"F63.wireOp",EDGE,"E99.sketch_text.stroke-0")}),-1.0]])]});
            var Q1;
            Q1=makeQuery(id+"F63.imprint","IMPRINT",FACE,{"disambiguationData":[TD([[makeQuery(id+"F63.imprint","IMPRINT",EDGE,{"derivedFrom":sQuery(id+"F63.wireOp",EDGE,"E99.sketch_text.stroke-9")}),-1.0]])]});
            extrude(context, id + "F97", {"entities" : qUnion([Q0, Q1]), "operationType" : NewBodyOperationType.REMOVE, "oppositeDirection" : true, "depth" : 0.25 * mm});
        }
        {
            var Q0;
            Q0=makeQuery(id+"F68.imprint","IMPRINT",FACE,{"disambiguationData":[TD([[makeQuery(id+"F68.imprint","IMPRINT",EDGE,{"derivedFrom":sQuery(id+"F68.wireOp",EDGE,"E104.sketch_text.stroke-9")}),-1.0]])]});
            var Q1;
            Q1=makeQuery(id+"F68.imprint","IMPRINT",FACE,{"disambiguationData":[TD([[makeQuery(id+"F68.imprint","IMPRINT",EDGE,{"derivedFrom":sQuery(id+"F68.wireOp",EDGE,"E104.sketch_text.stroke-0")}),-1.0]])]});
            extrude(context, id + "F98", {"entities" : qUnion([Q0, Q1]), "operationType" : NewBodyOperationType.REMOVE, "oppositeDirection" : true, "depth" : 0.25 * mm});
        }
        {
            var Q0;
            Q0=makeQuery(id+"F78.imprint","IMPRINT",FACE,{"disambiguationData":[TD([[makeQuery(id+"F78.imprint","IMPRINT",EDGE,{"derivedFrom":sQuery(id+"F78.wireOp",EDGE,"E113.sketch_text.stroke-0")}),-1.0]])]});
            var Q1;
            Q1=makeQuery(id+"F78.imprint","IMPRINT",FACE,{"disambiguationData":[TD([[makeQuery(id+"F78.imprint","IMPRINT",EDGE,{"derivedFrom":sQuery(id+"F78.wireOp",EDGE,"E113.sketch_text.stroke-26")}),-1.0]])]});
            extrude(context, id + "F99", {"entities" : qUnion([Q0, Q1]), "operationType" : NewBodyOperationType.REMOVE, "oppositeDirection" : true, "depth" : 0.25 * mm});
        }
        {
            var Q0;
            Q0=makeQuery(id+"F72.imprint","IMPRINT",FACE,{"disambiguationData":[TD([[makeQuery(id+"F72.imprint","IMPRINT",EDGE,{"derivedFrom":sQuery(id+"F72.wireOp",EDGE,"E107.sketch_text.stroke-0")}),-1.0]])]});
            extrude(context, id + "F100", {"entities" : qUnion([Q0]), "operationType" : NewBodyOperationType.REMOVE, "oppositeDirection" : true, "depth" : 0.25 * mm});
        }
        {
            var Q0;
            Q0=makeQuery(id+"F76.imprint","IMPRINT",FACE,{"disambiguationData":[TD([[makeQuery(id+"F76.imprint","IMPRINT",EDGE,{"derivedFrom":sQuery(id+"F76.wireOp",EDGE,"E111.sketch_text.stroke-0")}),-1.0]])]});
            extrude(context, id + "F101", {"entities" : qUnion([Q0]), "operationType" : NewBodyOperationType.REMOVE, "oppositeDirection" : true, "depth" : 0.25 * mm});
        }
        {
            var Q0;
            Q0=makeQuery(id+"F67.imprint","IMPRINT",FACE,{"disambiguationData":[TD([[makeQuery(id+"F67.imprint","IMPRINT",EDGE,{"derivedFrom":sQuery(id+"F67.wireOp",EDGE,"E103.sketch_text.stroke-0")}),-1.0]])]});
            extrude(context, id + "F102", {"entities" : qUnion([Q0]), "operationType" : NewBodyOperationType.REMOVE, "oppositeDirection" : true, "depth" : 0.25 * mm});
        }
        {
            var Q0;
            Q0=qCreatedBy(makeId("Top.planeOp"),FACE);
            cPlane(context, id + "F103", {"entities" : qUnion([Q0]), "cplaneType" : CPlaneType.OFFSET, "offset" : 7.72 * mm, "width" : 152.4 * mm, "height" : 152.4 * mm});
        }
    });
